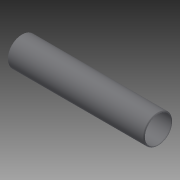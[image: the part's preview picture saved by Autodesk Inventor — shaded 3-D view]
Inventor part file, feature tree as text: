
AUTODESK INVENTOR PART (.ipt)
format: ipt  version: 2014 (Build 180170000, 170)  size: 145,408 bytes
history: native  units: in
note: dims shown in document units (in); Inventor stores cm internally (conversion verified against a paired STEP export)
features: other x42, revolve x1, sketch x1
ambient origin geometry x8: Origin, YZ Plane, XZ Plane, XY Plane, X Axis, Y Axis, Z Axis, Center Point
bodies: Solid1 (feature_tree)
feature tree (44):
  revolve  "Revolution1"  [1 undecoded]
  other  "cp1_XY"
  other  "cp1_YZ"
  other  "cp1_ZX"
  other  "cp1_X"
  other  "cp1_Y"
  other  "cp1_Z"
  other  "cp1_Center"
  other  "cp2_XY"
  other  "cp2_YZ"
  other  "cp2_ZX"
  other  "cp2_X"
  other  "cp2_Y"
  other  "cp2_Z"
  other  "cp2_Center"
  other  "cp3_XY"
  other  "cp3_YZ"
  other  "cp3_ZX"
  other  "cp3_X"
  other  "cp3_Y"
  other  "cp3_Z"
  other  "cp3_Center"
  other  "cp4_XY"
  other  "cp4_YZ"
  other  "cp4_ZX"
  other  "cp4_X"
  other  "cp4_Y"
  other  "cp4_Z"
  other  "cp4_Center"
  other  "tube_front_XY"
  other  "tube_front_YZ"
  other  "tube_front_ZX"
  other  "tube_front_X"
  other  "tube_front_Y"
  other  "tube_front_Z"
  other  "tube_front_Center"
  other  "tube_rear_XY"
  other  "tube_rear_YZ"
  other  "tube_rear_ZX"
  other  "tube_rear_X"
  other  "tube_rear_Y"
  other  "tube_rear_Z"
  other  "tube_rear_Center"
  sketch  "Sketch_1"  dims[d0=360.0deg]
note: 1 required parameter value undecoded (feature->parameter linkage not recoverable at this tier; creation-order binding heuristic only, values carry confidence <= 0.55)
